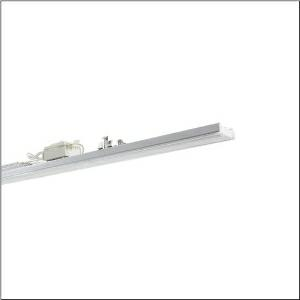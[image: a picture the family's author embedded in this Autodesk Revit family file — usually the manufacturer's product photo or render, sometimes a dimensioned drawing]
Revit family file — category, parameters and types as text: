
# Revit family: licross_21_recessed_mo_52te1ecn485g
name_source: partatom
category: Lighting Fixtures
units: mm (PartAtom-declared; Revit-internal decimal feet)

## family parameters
Cut with Voids When Loaded = No
Host = Face
Light Source = No
Part Type = Normal
Room Calculation Point = No
Round Connector Dimension = Use Diameter
Shared = No

## types (1)
- --- (1 x LED, 8960 lm, 49.9 W, 4000K)
    Apparent Load = 50 VA
    CIE Flux Codes = 85 95 99 100 100
    Color Rendering = 80
    Color Temperature = 4000K
    Default Elevation = 1800 mm
    Description = Licross 21 Recessed MO, luminaire insert, of sheet steel, galvanised, coil coated, white, length: 1.500mm, width: 66mm, height: 67mm, LED rated luminous flux: 8.960lm, light colour: 840, SDCM (Standard Deviation of Colour Matching)MacAdam ≤ 3 SDCM (initial), control gear: ON/OFF Multilumen, CLOi, with plug, 3-pole, with phase selection, mains connection: 220..240V, AC, 50/60Hz, start of lifetime: 50W, end of service life: 61W, internal wiring halogen-free, primary light control with lens, of plastic, primary optical cover: cover, of PMMA, light emission: direct distribution, primary light characteristic: symmetric, protection rating (complete): IP54, insulation class (complete): insulation class I (protective earthing), certification: CE, ENEC, VDE, UKCA, protection symbol: D if used in an environment with non-conductive dust loads with corresponding accessories, impact resistance: IK06, permissible ambient temperature for indoor applications: -35..+40°C, corresponds to IFS (International Featured Standards) requirements for safety and quality in the food industry, reducing of maximum allowable ambient temperature of 5°C with ceiling mounting, LABS conformity tested according to VDMA 24364:2018-05, The light source and the operating device comply with the requirements of the Ecodesign Regulation (EU) 2019/2020 and are replaceable in accordance with this regulation, packaging unit: 1 piece
    Height = 58 mm
    Lamp = 1 x LED
    Lamp Light Flux = 8960 lm
    Lamp Power = 49.9 W
    Lamp count = 1
    Length = 1500 mm
    Luminous efficacy = 180 lm/W
    Manufacturer = Siteco
    ModVariant = No
    Model = 52TE1ECN485G
    Mounting Place = Ceiling
    Mounting Type = Pendant
    Number of Poles = 1
    OnlyDefault = Yes
    Power Factor = 1
    Product Name = Licross 21 Recessed MO
    Product group = luminaire insert | ceiling pendant
    ProductGroupID = 901
    Protection Class = Protection class I
    Protection Degree = IP 54
    RLX_Detail_Level = 1
    RLX_Emergency_Light_Flux = 0 lm
    RLX_Emergency_Type = 0
    RLX_Emergency_Type_DB = No
    RlxData = <blob elided: 22673 chars, md5=29b4db36>
    Socket = socket
    Standby Power = 0 W
    System Light Flux = 8960 lm
    System Power = 50 W
    Type Comments = factory setting: luminous flux: 100 % | (A | C | E) | 116 mA
    Type Image = l_1296930.jpg
    URL = http://relux.com
    VarID = @adj_109793
    Voltage = 0 V
    Weight = 0.00 kg
    Width = 66 mm

## geometry (parser evidence)
native form markers: Blend x4, Sweep x10
no freeform markers — native parametric forms only
